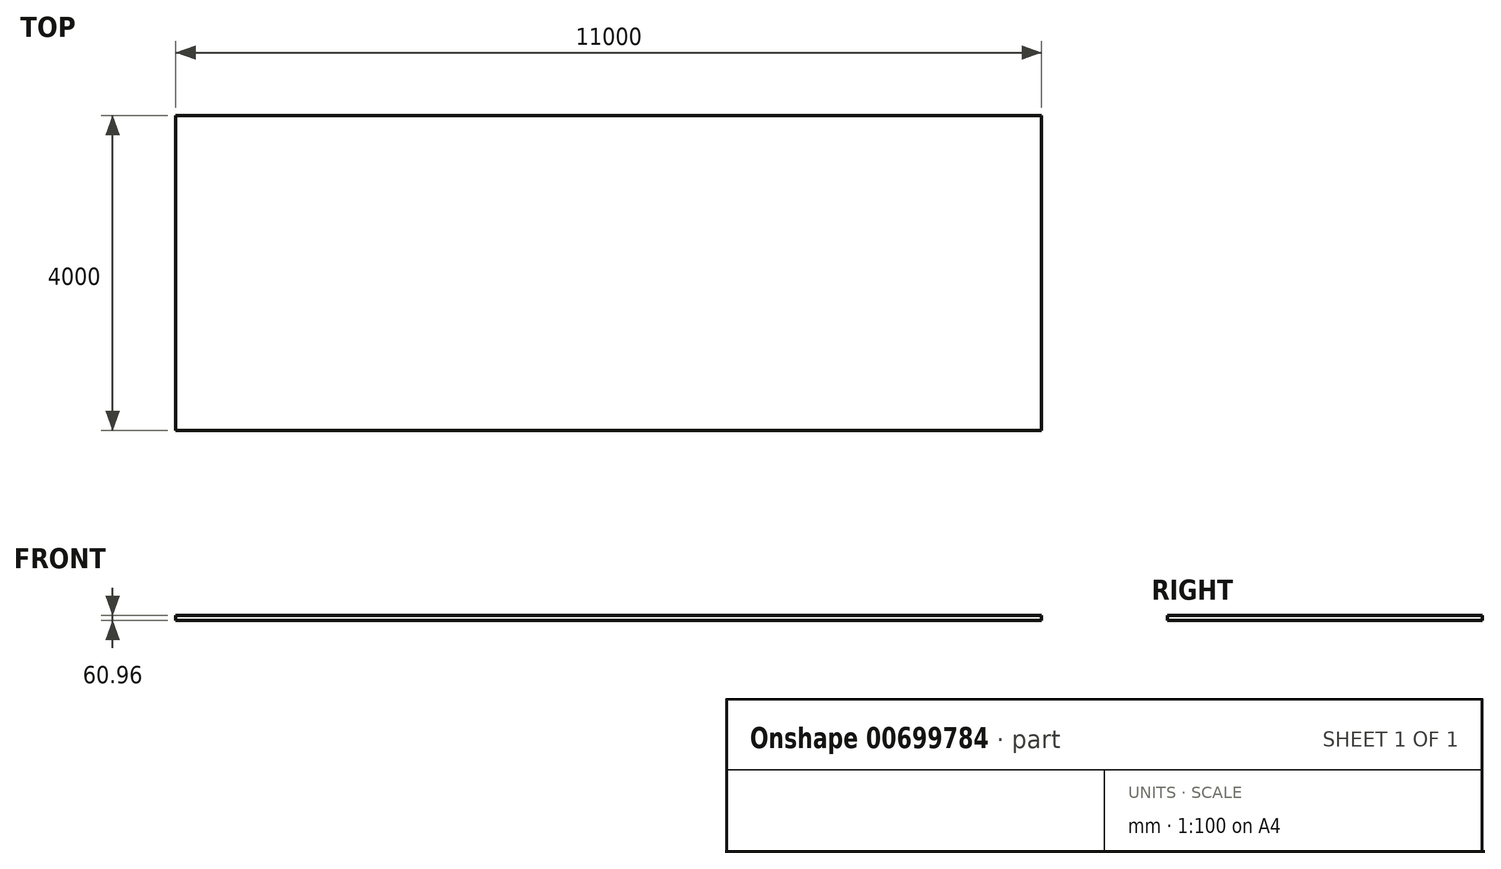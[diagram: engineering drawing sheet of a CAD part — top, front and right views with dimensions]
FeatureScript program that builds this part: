
annotation { "Feature Type Name" : "Feature", "Feature Type Description" : "" }
export const myFeature = defineFeature(function(context is Context, id is Id, definition is map)
    precondition{}
    {
        {
            var Q0;
            Q0=qCreatedBy(makeId("Top.planeOp"),FACE);
            var sketch = newSketch(context, id + "F0", { "sketchPlane" : qUnion([Q0])});
            skLineSegment(sketch, "E0.bottom", {"start": v(-5500, 2000) * mm, "end": v(5500, 2000) * mm});
            skLineSegment(sketch, "E0.top", {"start": v(-5500, -2000) * mm, "end": v(5500, -2000) * mm});
            skLineSegment(sketch, "E0.left", {"start": v(-5500, 2000) * mm, "end": v(-5500, -2000) * mm});
            skLineSegment(sketch, "E0.right", {"start": v(5500, 2000) * mm, "end": v(5500, -2000) * mm});
            skPoint(sketch, "E0.middle", {"position": v(0, 0) * mm});
            skSolve(sketch);
        }
        {
            var Q0;
            Q0=makeQuery(id+"F0.imprint","IMPRINT",FACE,{"disambiguationData":[TD([[makeQuery(id+"F0.imprint","IMPRINT",EDGE,{"derivedFrom":sQuery(id+"F0.wireOp",EDGE,"E0.bottom")}),-1.0]])]});
            extrude(context, id + "F1", {"entities" : qUnion([Q0]), "depth" : 60.96 * mm});
        }
        {
            var Q0;
            Q0=makeQuery(id+"F1.opExtrude","SWEPT_FACE",FACE,{"disambiguationData":[OSD([sQuery(id+"F0.wireOp",EDGE,"E0.right")])]});
            var sketch = newSketch(context, id + "F2", { "sketchPlane" : qUnion([Q0])});
            skLineSegment(sketch, "E1.bottom", {"start": v(-2000, 60.96) * mm, "end": v(2000, 60.96) * mm});
            skLineSegment(sketch, "E1.top", {"start": v(-2000, 60.96) * mm, "end": v(2000, 60.96) * mm});
            skLineSegment(sketch, "E1.left", {"start": v(-2000, 60.96) * mm, "end": v(-2000, 60.96) * mm});
            skLineSegment(sketch, "E1.right", {"start": v(2000, 60.96) * mm, "end": v(2000, 60.96) * mm});
            skLineSegment(sketch, "E2.bottom", {"start": v(2000, 2015.96) * mm, "end": v(-2000, 2015.96) * mm});
            skLineSegment(sketch, "E2.top", {"start": v(2000, 60.96) * mm, "end": v(-2000, 60.96) * mm});
            skLineSegment(sketch, "E2.left", {"start": v(2000, 2015.96) * mm, "end": v(2000, 60.96) * mm});
            skLineSegment(sketch, "E2.right", {"start": v(-2000, 2015.96) * mm, "end": v(-2000, 60.96) * mm});
            skSolve(sketch);
        }
        {
            var Q0;
            Q0=makeQuery(id+"F2.imprint","IMPRINT",FACE,{"disambiguationData":[TD([[makeQuery(id+"F2.imprint","IMPRINT",EDGE,{"derivedFrom":sQuery(id+"F2.wireOp",EDGE,"E2.bottom")}),1.0]])]});
            extrude(context, id + "F3", {"entities" : qUnion([Q0]), "depth" : 30.48 * mm});
        }
        {
            var Q0;
            Q0=makeQuery(id+"F3.opExtrude","SWEPT_BODY",BODY,{"disambiguationData":[OSD([sQuery(id+"F2.wireOp",EDGE,"E2.bottom"),sQuery(id+"F2.wireOp",EDGE,"E2.top"),sQuery(id+"F2.wireOp",EDGE,"E2.left"),sQuery(id+"F2.wireOp",EDGE,"E2.right")])]});
            deleteBodies(context, id + "F4", {"entities" : qUnion([Q0])});
        }
    });
